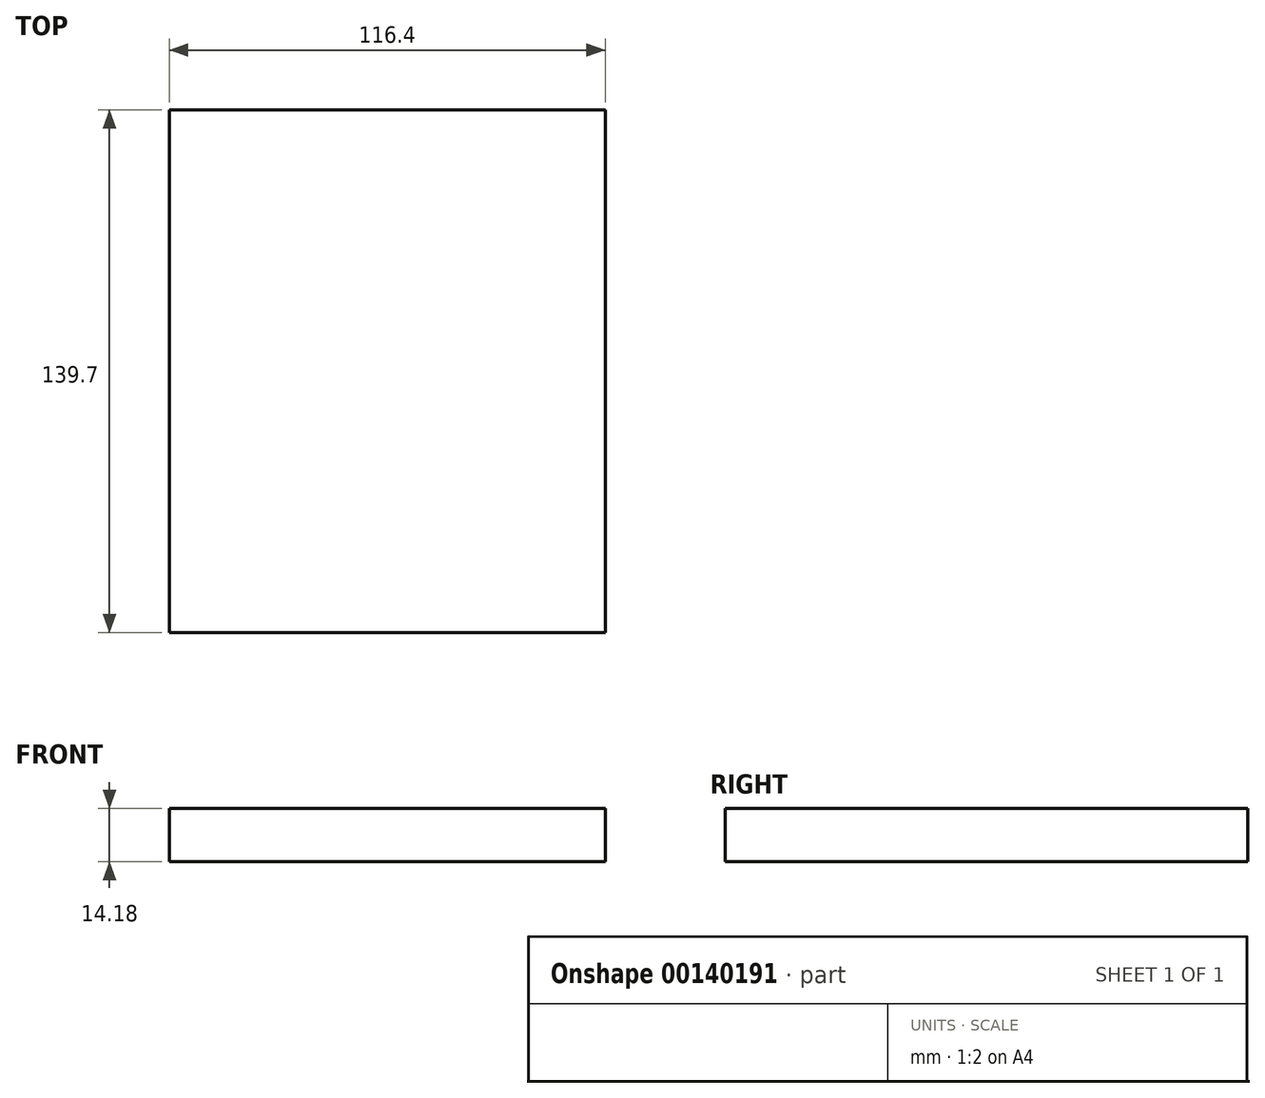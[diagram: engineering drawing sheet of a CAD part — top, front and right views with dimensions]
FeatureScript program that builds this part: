
annotation { "Feature Type Name" : "Feature", "Feature Type Description" : "" }
export const myFeature = defineFeature(function(context is Context, id is Id, definition is map)
    precondition{}
    {
        {
            var Q0;
            Q0=qCreatedBy(makeId("Front.planeOp"),FACE);
            var sketch = newSketch(context, id + "F0", { "sketchPlane" : qUnion([Q0])});
            skLineSegment(sketch, "E0.bottom", {"start": v(-58.2, -22.78) * mm, "end": v(58.2, -22.78) * mm});
            skLineSegment(sketch, "E0.top", {"start": v(-58.2, -36.96) * mm, "end": v(58.2, -36.96) * mm});
            skLineSegment(sketch, "E0.left", {"start": v(-58.2, -22.78) * mm, "end": v(-58.2, -36.96) * mm});
            skLineSegment(sketch, "E0.right", {"start": v(58.2, -22.78) * mm, "end": v(58.2, -36.96) * mm});
            skPoint(sketch, "E1", {"position": v(0, -36.96) * mm});
            skSolve(sketch);
        }
        {
            var Q0;
            Q0=qSketchRegion(id+"F0",true);
            extrude(context, id + "F1", {"entities" : qUnion([Q0]), "depth" : 139.7 * mm});
        }
        {
            var Q0;
            Q0=qCreatedBy(makeId("Right.planeOp"),FACE);
            cPlane(context, id + "F2", {"entities" : qUnion([Q0]), "cplaneType" : CPlaneType.OFFSET, "offset" : 28.1 * mm, "oppositeDirection" : true, "width" : 152.4 * mm, "height" : 152.4 * mm});
        }
        {
            var Q0;
            Q0=makeQuery(id+"F1.opExtrude","SWEPT_FACE",FACE,{"disambiguationData":[OSD([sQuery(id+"F0.wireOp",EDGE,"E0.top")])]});
            var sketch = newSketch(context, id + "F3", { "sketchPlane" : qUnion([Q0])});
            skLineSegment(sketch, "E2.bottom", {"start": v(-38.73, 118.78) * mm, "end": v(38.73, 118.78) * mm});
            skLineSegment(sketch, "E2.top", {"start": v(-38.73, 42.58) * mm, "end": v(38.73, 42.58) * mm});
            skLineSegment(sketch, "E2.left", {"start": v(-38.74, 118.78) * mm, "end": v(-38.74, 42.58) * mm});
            skLineSegment(sketch, "E2.right", {"start": v(38.73, 118.78) * mm, "end": v(38.73, 42.58) * mm});
            skPoint(sketch, "E3", {"position": v(0, 118.78) * mm});
            skLineSegment(sketch, "E4.bottom", {"start": v(-58.2, 0) * mm, "end": v(-32.8, 0) * mm});
            skLineSegment(sketch, "E4.top", {"start": v(-58.2, 38.1) * mm, "end": v(-32.8, 38.1) * mm});
            skLineSegment(sketch, "E4.left", {"start": v(-58.2, 0) * mm, "end": v(-58.2, 38.1) * mm});
            skLineSegment(sketch, "E4.right", {"start": v(-32.8, 0) * mm, "end": v(-32.8, 38.1) * mm});
            skLineSegment(sketch, "E5.bottom", {"start": v(58.2, 0) * mm, "end": v(32.8, 0) * mm});
            skLineSegment(sketch, "E5.top", {"start": v(58.2, 38.1) * mm, "end": v(32.8, 38.1) * mm});
            skLineSegment(sketch, "E5.left", {"start": v(58.2, 0) * mm, "end": v(58.2, 38.1) * mm});
            skLineSegment(sketch, "E5.right", {"start": v(32.8, 0) * mm, "end": v(32.8, 38.1) * mm});
            skSolve(sketch);
        }
    });
